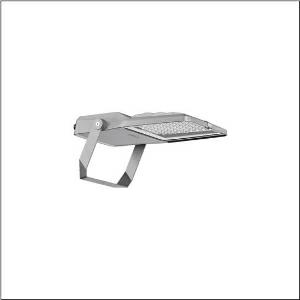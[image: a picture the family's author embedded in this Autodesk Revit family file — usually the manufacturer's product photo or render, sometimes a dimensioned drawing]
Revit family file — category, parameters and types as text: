
# Revit family: floodlight_fl_21_mini___pl43_5xa7774c4a1a_6312
name_source: partatom
category: Lighting Fixtures
units: mm (PartAtom-declared; Revit-internal decimal feet)

## family parameters
Cut with Voids When Loaded = No
Host = Face
Light Source = No
Part Type = Normal
Room Calculation Point = No
Round Connector Dimension = Use Diameter
Shared = No

## types (1)
- --- (1 x LED, 13000 lm, 88.8 W, 4000K)
    Apparent Load = 89 VA
    CIE Flux Codes = 27 78 99 100 100
    Color Rendering = 70
    Color Temperature = 4000K
    Default Elevation = 1800 mm
    Description = Floodlight FL 21 mini, floodlight, primary light control with lens, of PMMA, primary optical cover: protective disc, of toughened safety glass, transparent, light distribution: PL43, light emission: direct distribution, installation type: surface-mounted, LED, High Power LED, rated luminous flux: 13.000lm, luminous efficacy: 146lm/W, light colour: 740, colour temperature: 4000K, control gear: DALI 2, control: overheat protection, power reduction, constant luminous flux control, flexible luminous flux parameterisation, pre-setting: linear dimming characteristic, with terminal, 6-pole, mains connection: 220..240V, AC/DC, 0/50..60Hz, start of lifetime: 89W, end of service life: 94W, reduction: 42W, luminaire housing, of diecast aluminium, powder-coated, SITECO metallic grey (DB 702S), corrosivity category C5 mid according to DIN EN ISO 12944, chlorine-resistant, suitable for swimming pools, sealing non-destructively replaceable, mounting bracket, of steel, galvanised, powder-coated, SITECO metallic grey (DB 702S), protection rating (complete): IP66, insulation class (complete): insulation class II (safety insulation), certification: CE, ENEC, VDE, impact resistance: IK08, permissible operating ambient temperature: -40..+40°C, permissible operating ambient temperature for outdoor applications: -40..+50°C, standard: DIN EN 12944, LABS conformity tested according to VDMA 24364:2018-05, packaging unit: 1 piece

Light Distribution: PL43
    Height = 70 mm
    Lamp = 1 x LED
    Lamp Light Flux = 13000 lm
    Lamp Power = 88.8 W
    Lamp count = 1
    Length = 485 mm
    Luminous efficacy = 146 lm/W
    Manufacturer = Siteco
    ModVariant = No
    Model = 5XA7774C4A1A
    Number of Poles = 1
    OnlyDefault = Yes
    Power Factor = 1
    Product Name = Floodlight FL 21 mini | PL43
    Product group = floodlight | pylon annexe
    ProductGroupID = 6201
    Protection Class = Protection class II
    Protection Degree = IP 66
    RLX_Detail_Level = 1
    RLX_Emergency_Light_Flux = 0 lm
    RLX_Emergency_Type = 0
    RLX_Emergency_Type_DB = No
    RlxData = <blob elided: 96001 chars, md5=13861ef3>
    Socket = socket
    Standby Power = 0 W
    System Light Flux = 13000 lm
    System Power = 89 W
    Type Comments = factory setting: luminous flux: 100 % | dim-lin: 254 | 456 mA
    Type Image = l_1006845.jpg
    URL = http://relux.com
    VarID = @adj_161011
    Voltage = 0 V
    Weight = 0.00 kg
    Width = 337 mm

## geometry (parser evidence)
native form markers: Blend x4, Sweep x12
no freeform markers — native parametric forms only
